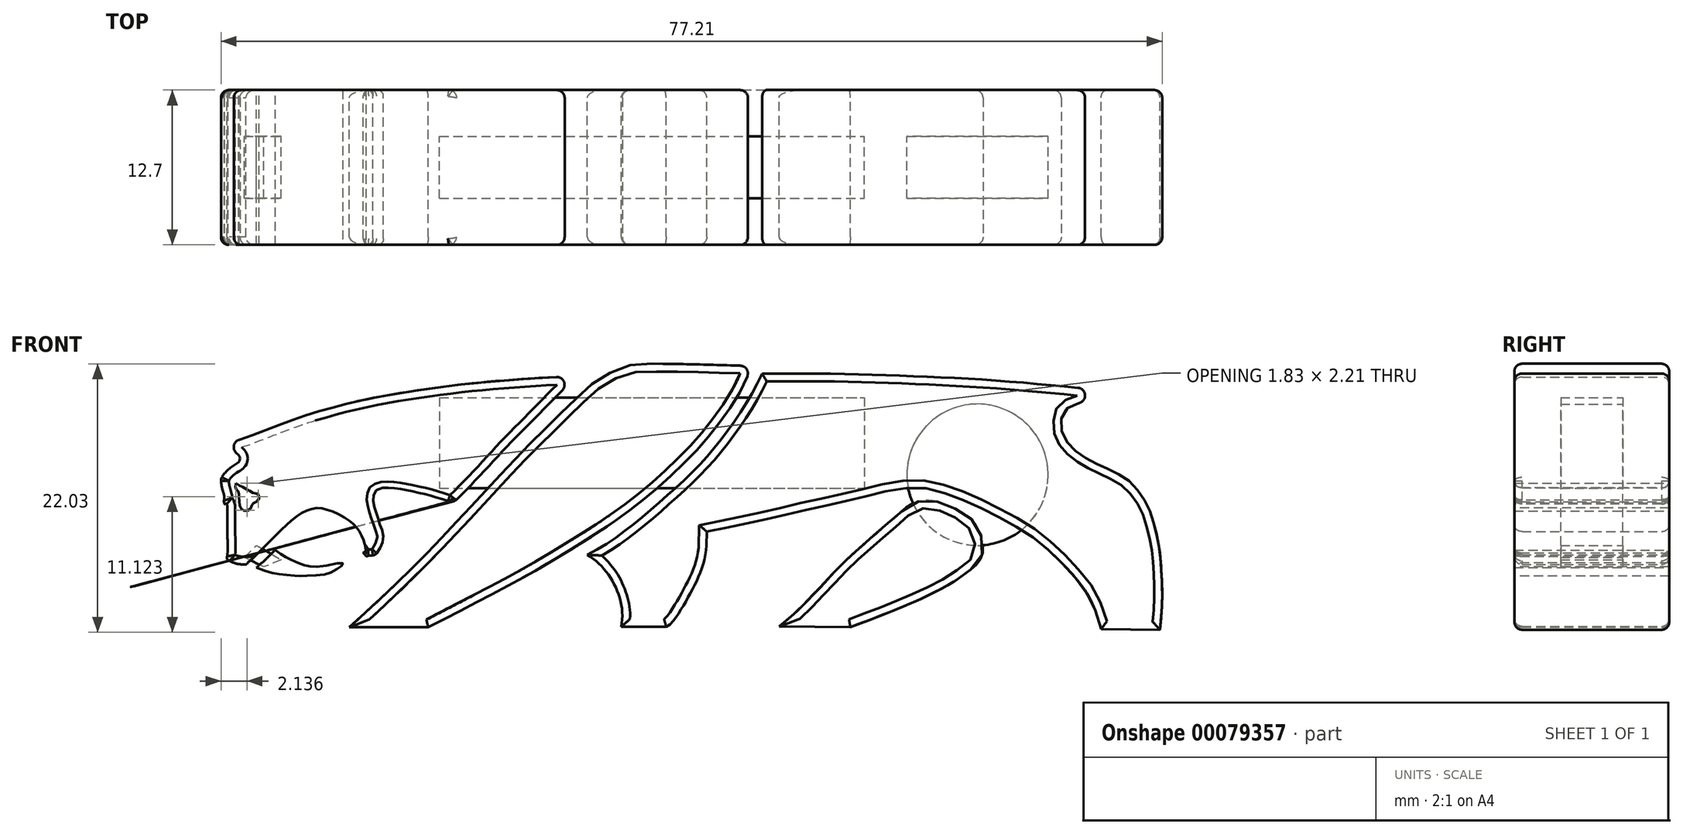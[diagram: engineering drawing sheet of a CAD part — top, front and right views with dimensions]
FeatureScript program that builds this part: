
annotation { "Feature Type Name" : "Feature", "Feature Type Description" : "" }
export const myFeature = defineFeature(function(context is Context, id is Id, definition is map)
    precondition{}
    {
        {
            var Q0;
            Q0=qCreatedBy(makeId("Front.planeOp"),FACE);
            var sketch = newSketch(context, id + "F0", { "sketchPlane" : qUnion([Q0])});
            skFitSpline(sketch, "E0", {"points": [v(-38.9, 16.63) * mm, v(-38.37, 16.66) * mm, v(-37.5, 16.88) * mm, v(-34.83, 17.89) * mm, v(-32.87, 18.61) * mm, v(-30.82, 19.24) * mm, v(-28.43, 19.87) * mm, v(-25.9, 20.4) * mm, v(-23.7, 20.77) * mm, v(-20.63, 21.2) * mm, v(-18, 21.5) * mm, v(-15.26, 21.73) * mm, v(-10.09, 22.05) * mm, v(-10.06, 22.05) * mm], "startDerivative": vector(13.14, 0.1) * mm, "endDerivative": vector(1.31, -0.1) * mm});
            skFitSpline(sketch, "E1", {"points": [v(-20.18, 11.64) * mm, v(-18.27, 13.57) * mm, v(-16.09, 15.93) * mm, v(-13.45, 18.61) * mm, v(-12.15, 19.94) * mm, v(-10.06, 22.05) * mm], "startDerivative": vector(9.83, 9.74) * mm, "endDerivative": vector(11.12, 11.22) * mm});
            skFitSpline(sketch, "E2", {"points": [v(-37.18, 6.58) * mm, v(-35.83, 7.86) * mm, v(-34.37, 9.34) * mm, v(-33.64, 10) * mm, v(-32.91, 10.62) * mm, v(-32.26, 10.97) * mm, v(-31.76, 11.15) * mm, v(-31.13, 11.2) * mm, v(-30.53, 11.07) * mm, v(-29.85, 10.82) * mm, v(-28.97, 10.34) * mm, v(-28.52, 10.02) * mm, v(-28.05, 9.54) * mm, v(-27.85, 9.24) * mm, v(-27.6, 8.75) * mm, v(-27.46, 8.36) * mm, v(-27.37, 7.82) * mm, v(-27.39, 7.68) * mm, v(-27.56, 7.54) * mm], "startDerivative": vector(14.42, 13.18) * mm, "endDerivative": vector(-7, -4.12) * mm});
            skFitSpline(sketch, "E3", {"points": [v(-20.18, 11.64) * mm, v(-20.88, 11.87) * mm, v(-21.7, 12.12) * mm, v(-22.69, 12.4) * mm, v(-23.57, 12.58) * mm, v(-24.22, 12.72) * mm, v(-24.83, 12.8) * mm, v(-25.45, 12.87) * mm, v(-25.85, 12.88) * mm, v(-26.1, 12.82) * mm, v(-26.4, 12.72) * mm, v(-26.62, 12.6) * mm, v(-26.7, 12.4) * mm, v(-26.76, 12.12) * mm, v(-26.76, 11.8) * mm, v(-26.7, 11.44) * mm, v(-26.6, 11.12) * mm, v(-26.42, 10.54) * mm, v(-26.22, 9.94) * mm, v(-26.03, 9.42) * mm, v(-25.92, 9.1) * mm, v(-25.9, 8.78) * mm, v(-25.94, 8.5) * mm, v(-26.07, 8.2) * mm, v(-26.22, 7.85) * mm, v(-26.36, 7.65) * mm, v(-26.5, 7.45) * mm, v(-26.62, 7.36) * mm, v(-26.76, 7.33) * mm, v(-26.98, 7.3) * mm, v(-27.18, 7.29) * mm, v(-27.3, 7.26) * mm, v(-27.56, 7.54) * mm], "startDerivative": vector(-16.05, 5.29) * mm, "endDerivative": vector(-9.29, 12.72) * mm});
            skFitSpline(sketch, "E4", {"points": [v(-38, 13.24) * mm, v(-37.74, 13.04) * mm, v(-37.46, 12.91) * mm, v(-37.1, 12.72) * mm, v(-36.85, 12.62) * mm, v(-36.64, 12.46) * mm, v(-36.32, 12.4) * mm, v(-36.19, 12.35) * mm, v(-36.12, 12.18) * mm, v(-36.13, 11.89) * mm, v(-36.4, 11.69) * mm, v(-36.65, 11.53) * mm, v(-36.72, 11.4) * mm, v(-36.8, 11.18) * mm, v(-37, 11.01) * mm, v(-37.25, 10.97) * mm, v(-37.5, 11.07) * mm, v(-37.65, 11.3) * mm, v(-37.74, 11.56) * mm, v(-37.75, 12) * mm, v(-37.8, 12.28) * mm, v(-37.77, 12.45) * mm, v(-37.85, 12.6) * mm, v(-37.95, 12.66) * mm, v(-38, 12.8) * mm, v(-38.03, 12.93) * mm, v(-38, 13.24) * mm]});
            skFitSpline(sketch, "E5", {"points": [v(-38.9, 16.63) * mm, v(-38.72, 16.34) * mm, v(-38.31, 15.96) * mm, v(-38.04, 15.75) * mm, v(-37.79, 15.56) * mm, v(-37.7, 15.35) * mm, v(-37.68, 15.2) * mm, v(-37.79, 15) * mm, v(-37.93, 14.86) * mm, v(-38.46, 14.5) * mm, v(-38.9, 14.11) * mm, v(-39.09, 13.86) * mm, v(-39.17, 13.71) * mm, v(-39.23, 13.56) * mm, v(-39.2, 13.06) * mm, v(-39.13, 12.8) * mm, v(-39.03, 12.4) * mm, v(-38.97, 12.12) * mm, v(-38.98, 11.6) * mm, v(-38.9, 11.53) * mm, v(-38.79, 11.59) * mm, v(-38.72, 10.31) * mm, v(-38.72, 7.29) * mm, v(-38.72, 7) * mm, v(-38.1, 6.7) * mm, v(-37.74, 6.6) * mm, v(-37.18, 6.58) * mm], "startDerivative": vector(3.81, -8.13) * mm, "endDerivative": vector(13.6, -0.25) * mm});
            skFitSpline(sketch, "E6", {"points": [v(-34.8, 7.76) * mm, v(-34.12, 7.3) * mm, v(-33.5, 6.96) * mm, v(-32.6, 6.57) * mm, v(-31.95, 6.42) * mm, v(-30.83, 6.44) * mm, v(-29.26, 6.7) * mm, v(-29.27, 6.57) * mm, v(-29.4, 6.4) * mm, v(-30.11, 5.98) * mm, v(-30.92, 5.74) * mm, v(-32.35, 5.65) * mm, v(-33, 5.65) * mm, v(-34.14, 5.75) * mm, v(-35.06, 5.9) * mm, v(-36.33, 6.33) * mm], "startDerivative": vector(10.38, -7.41) * mm, "endDerivative": vector(-15.79, 5.96) * mm});
            skFitSpline(sketch, "E7", {"points": [v(4.24, 22.85) * mm, v(3.48, 20.98) * mm, v(1.1, 17.49) * mm, v(-1.44, 14.7) * mm, v(-4.3, 12.12) * mm, v(-7.57, 9.7) * mm, v(-9.68, 8.34) * mm, v(-11.33, 7.33) * mm, v(-14.15, 5.67) * mm, v(-22.23, 1.42) * mm], "startDerivative": vector(-6.95, -21) * mm, "endDerivative": vector(-51.72, -26.65) * mm});
            skFitSpline(sketch, "E8", {"points": [v(-22.23, 1.42) * mm, v(-28.7, 1.42) * mm], "startDerivative": vector(-6.47, 0) * mm, "endDerivative": vector(-6.47, 0) * mm});
            skFitSpline(sketch, "E9", {"points": [v(-28.7, 1.42) * mm, v(-24.45, 5.4) * mm, v(-19.19, 10.82) * mm, v(-15.4, 14.92) * mm, v(-12.46, 17.9) * mm, v(-10.41, 19.89) * mm, v(-9.13, 21.07) * mm, v(-8.73, 21.45) * mm, v(-8.2, 21.81) * mm, v(-7.57, 22.17) * mm, v(-7.02, 22.45) * mm, v(-6.24, 22.74) * mm, v(-5.78, 22.89) * mm, v(-4.91, 23.02) * mm, v(4.24, 22.85) * mm], "startDerivative": vector(36.28, 33.23) * mm, "endDerivative": vector(81.45, -2.6) * mm});
            skFitSpline(sketch, "E10", {"points": [v(-6.4, 1.46) * mm, v(-6.31, 2.33) * mm, v(-6.37, 3.13) * mm, v(-6.58, 4) * mm, v(-6.9, 4.8) * mm, v(-7.41, 5.7) * mm, v(-7.9, 6.3) * mm, v(-8.3, 6.74) * mm, v(-9.18, 7.37) * mm], "startDerivative": vector(0.97, 6.96) * mm, "endDerivative": vector(-6.9, 4.6) * mm});
            skFitSpline(sketch, "E11", {"points": [v(-9.18, 7.37) * mm, v(-7.44, 8.37) * mm, v(-5.91, 9.47) * mm, v(-4.28, 10.78) * mm, v(-1.95, 12.86) * mm, v(-0.32, 14.39) * mm, v(1.21, 16.1) * mm, v(2.62, 17.95) * mm, v(3.75, 19.6) * mm, v(4.43, 20.81) * mm, v(5.15, 22.24) * mm], "startDerivative": vector(18, 9.78) * mm, "endDerivative": vector(8.35, 16.75) * mm});
            skFitSpline(sketch, "E12", {"points": [v(-6.4, 1.46) * mm, v(-2.72, 1.46) * mm], "startDerivative": vector(3.68, 0) * mm, "endDerivative": vector(3.68, 0) * mm});
            skFitSpline(sketch, "E13", {"points": [v(-2.72, 1.46) * mm, v(-2.37, 1.69) * mm, v(-1.84, 2.34) * mm, v(-1.34, 3.13) * mm, v(-0.94, 3.84) * mm, v(-0.56, 4.56) * mm, v(-0.2, 5.25) * mm, v(0.25, 6.4) * mm, v(0.53, 7.47) * mm, v(0.61, 9.28) * mm], "startDerivative": vector(4.66, 2.38) * mm, "endDerivative": vector(0.17, 12.66) * mm});
            skFitSpline(sketch, "E14", {"points": [v(0.61, 9.28) * mm, v(2.65, 9.7) * mm, v(5.56, 10.3) * mm, v(8.97, 11.11) * mm, v(11.35, 11.61) * mm, v(14.12, 12.29) * mm, v(15.87, 12.7) * mm, v(16.6, 12.8) * mm, v(17.41, 12.83) * mm, v(18.3, 12.85) * mm, v(18.73, 12.82) * mm, v(19.2, 12.72) * mm, v(20.12, 12.43) * mm, v(21.28, 12.01) * mm, v(22.59, 11.46) * mm, v(23.83, 10.86) * mm, v(25.1, 10.2) * mm, v(26.3, 9.51) * mm, v(27.1, 9) * mm, v(27.87, 8.44) * mm, v(28.73, 7.68) * mm, v(29.74, 6.73) * mm, v(30.28, 6.15) * mm, v(30.83, 5.53) * mm, v(31.5, 4.68) * mm, v(32, 3.9) * mm, v(32.42, 3) * mm, v(32.97, 1.28) * mm], "startDerivative": vector(42, 8.64) * mm, "endDerivative": vector(12.4, -42.68) * mm});
            skFitSpline(sketch, "E15", {"points": [v(5.15, 22.24) * mm, v(6.89, 22.24) * mm, v(8.36, 22.24) * mm, v(10.18, 22.24) * mm, v(13.52, 22.16) * mm, v(16.4, 22.07) * mm, v(19.27, 21.95) * mm, v(22.2, 21.8) * mm, v(27.17, 21.44) * mm, v(34, 20.77) * mm], "startDerivative": vector(21.12, 0.01) * mm, "endDerivative": vector(41.87, -4.26) * mm});
            skFitSpline(sketch, "E16", {"points": [v(34, 20.77) * mm, v(33.94, 20.57) * mm, v(33.89, 20.47) * mm, v(33.7, 20.33) * mm, v(33.1, 20.17) * mm, v(32.24, 20.02) * mm, v(31.57, 19.9) * mm, v(30.76, 19.7) * mm, v(30.04, 19.29) * mm, v(29.83, 19) * mm, v(29.74, 18.74) * mm, v(29.7, 18.29) * mm, v(29.7, 18) * mm, v(29.73, 17.59) * mm, v(29.81, 17.24) * mm, v(30, 16.86) * mm, v(30.23, 16.52) * mm, v(30.64, 16.11) * mm, v(30.93, 15.86) * mm, v(31.31, 15.57) * mm, v(31.85, 15.24) * mm, v(32.57, 14.84) * mm, v(33.26, 14.53) * mm, v(33.72, 14.3) * mm, v(34.26, 14.05) * mm, v(34.8, 13.74) * mm, v(35.2, 13.47) * mm, v(35.55, 13.14) * mm, v(35.9, 12.74) * mm, v(36.24, 12.3) * mm, v(36.5, 11.9) * mm, v(36.81, 11.39) * mm, v(37.03, 10.8) * mm, v(37.16, 10.4) * mm, v(37.38, 9.6) * mm, v(37.62, 8.6) * mm, v(37.83, 7.27) * mm, v(37.94, 5.54) * mm, v(37.98, 4.1) * mm, v(37.8, 1.22) * mm], "startDerivative": vector(-3.18, -15.16) * mm, "endDerivative": vector(-4.8, -56.57) * mm});
            skFitSpline(sketch, "E17", {"points": [v(32.97, 1.28) * mm, v(37.8, 1.22) * mm], "startDerivative": vector(4.82, -0.06) * mm, "endDerivative": vector(4.82, -0.06) * mm});
            skFitSpline(sketch, "E18", {"points": [v(6.55, 1.5) * mm, v(12.4, 1.44) * mm], "startDerivative": vector(5.84, -0.06) * mm, "endDerivative": vector(5.84, -0.06) * mm});
            skFitSpline(sketch, "E19", {"points": [v(6.55, 1.5) * mm, v(7.94, 2.67) * mm, v(9.03, 3.77) * mm, v(9.91, 4.69) * mm, v(10.63, 5.46) * mm, v(11.13, 6) * mm, v(11.6, 6.5) * mm, v(13.08, 7.87) * mm, v(13.93, 8.63) * mm, v(14.71, 9.3) * mm, v(15.39, 9.9) * mm, v(15.97, 10.39) * mm, v(16.42, 10.76) * mm, v(17.02, 11.3) * mm, v(17.46, 11.56) * mm, v(18.12, 11.8) * mm, v(18.72, 11.86) * mm, v(19.36, 11.77) * mm, v(19.82, 11.63) * mm, v(20.37, 11.44) * mm, v(20.94, 11.19) * mm, v(21.69, 10.76) * mm, v(22.18, 10.42) * mm, v(22.6, 10.02) * mm, v(22.95, 9.38) * mm, v(23.14, 8.84) * mm, v(23.25, 8.37) * mm, v(23.28, 7.82) * mm, v(23.16, 7.23) * mm, v(22.72, 6.54) * mm, v(21.88, 5.86) * mm, v(20.7, 5.05) * mm, v(19.4, 4.36) * mm, v(17.84, 3.6) * mm, v(16.28, 2.95) * mm, v(14.98, 2.41) * mm, v(13.84, 1.99) * mm, v(12.4, 1.44) * mm], "startDerivative": vector(38.08, 30.48) * mm, "endDerivative": vector(-42.7, -16.34) * mm});
            skFitSpline(sketch, "E20", {"points": [v(-36.33, 6.33) * mm, v(-35.73, 6.85) * mm, v(-35.3, 7.25) * mm, v(-34.8, 7.76) * mm], "startDerivative": vector(1.8, 1.52) * mm, "endDerivative": vector(1.56, 1.6) * mm});
            skSolve(sketch);
        }
        {
            var Q0;
            Q0=makeQuery(id+"F0.imprint","IMPRINT",FACE,{"disambiguationData":[TD([[makeQuery(id+"F0.imprint","IMPRINT",EDGE,{"derivedFrom":sQuery(id+"F0.wireOp",EDGE,"E0")}),-1.0]])]});
            var Q1;
            Q1=makeQuery(id+"F0.imprint","IMPRINT",FACE,{"disambiguationData":[TD([[makeQuery(id+"F0.imprint","IMPRINT",EDGE,{"derivedFrom":sQuery(id+"F0.wireOp",EDGE,"E7")}),-1.0]])]});
            var Q2;
            Q2=makeQuery(id+"F0.imprint","IMPRINT",FACE,{"disambiguationData":[TD([[makeQuery(id+"F0.imprint","IMPRINT",EDGE,{"derivedFrom":sQuery(id+"F0.wireOp",EDGE,"E10")}),-1.0]])]});
            var Q3;
            Q3=makeQuery(id+"F0.imprint","IMPRINT",FACE,{"disambiguationData":[TD([[makeQuery(id+"F0.imprint","IMPRINT",EDGE,{"derivedFrom":sQuery(id+"F0.wireOp",EDGE,"E18")}),1.0]])]});
            var Q4;
            Q4=makeQuery(id+"F0.imprint","IMPRINT",FACE,{"disambiguationData":[TD([[makeQuery(id+"F0.imprint","IMPRINT",EDGE,{"derivedFrom":sQuery(id+"F0.wireOp",EDGE,"E6")}),-1.0]])]});
            extrude(context, id + "F1", {"entities" : qUnion([Q0, Q1, Q2, Q3, Q4]), "depth" : 6.35 * mm, "hasSecondDirection" : true, "secondDirectionOppositeDirection" : true, "secondDirectionDepth" : 6.35 * mm});
        }
        {
            var Q0;
            Q0=qCreatedBy(makeId("Front.planeOp"),FACE);
            var sketch = newSketch(context, id + "F2", { "sketchPlane" : qUnion([Q0])});
            skLineSegment(sketch, "E21.bottom", {"start": v(-21.31, 20.27) * mm, "end": v(13.55, 20.27) * mm});
            skLineSegment(sketch, "E21.top", {"start": v(-21.31, 12.84) * mm, "end": v(13.55, 12.84) * mm});
            skLineSegment(sketch, "E21.left", {"start": v(-21.31, 20.27) * mm, "end": v(-21.31, 12.84) * mm});
            skLineSegment(sketch, "E21.right", {"start": v(13.55, 20.27) * mm, "end": v(13.55, 12.84) * mm});
            skCircle(sketch, "E22", {"center": v(22.83, 13.94) * mm, "radius": 5.8 * mm});
            skLineSegment(sketch, "E23", {"start": v(-35.72, 6.37) * mm, "end": v(-37.33, 7.16) * mm});
            skLineSegment(sketch, "E24", {"start": v(-37.33, 7.16) * mm, "end": v(-36.32, 8.14) * mm});
            skLineSegment(sketch, "E25", {"start": v(-36.32, 8.14) * mm, "end": v(-34.3, 6.97) * mm});
            skLineSegment(sketch, "E26", {"start": v(-34.3, 6.97) * mm, "end": v(-35.72, 6.37) * mm});
            skSolve(sketch);
        }
        {
            var Q0;
            Q0=makeQuery(id+"F2.imprint","IMPRINT",FACE,{"disambiguationData":[TD([[makeQuery(id+"F2.imprint","IMPRINT",EDGE,{"derivedFrom":sQuery(id+"F2.wireOp",EDGE,"E21.bottom")}),-1.0]])]});
            var Q1;
            Q1=makeQuery(id+"F2.imprint","IMPRINT",FACE,{"disambiguationData":[TD([[makeQuery(id+"F2.imprint","IMPRINT",EDGE,{"derivedFrom":sQuery(id+"F2.wireOp",EDGE,"E22")}),1.0]])]});
            var Q2;
            Q2=makeQuery(id+"F2.imprint","IMPRINT",FACE,{"disambiguationData":[TD([[makeQuery(id+"F2.imprint","IMPRINT",EDGE,{"derivedFrom":sQuery(id+"F2.wireOp",EDGE,"E23")}),-1.0]])]});
            extrude(context, id + "F3", {"entities" : qUnion([Q0, Q1, Q2]), "depth" : 2.54 * mm, "hasSecondDirection" : true, "secondDirectionOppositeDirection" : true, "secondDirectionDepth" : 2.54 * mm});
        }
        {
            var Q0;
            Q0=makeQuery(id+"F1.opExtrude","CAP_EDGE",EDGE,{"disambiguationData":[OSD([sQuery(id+"F0.wireOp",EDGE,"E9")])],"isStart":false});
            var Q1;
            Q1=makeQuery(id+"F1.opExtrude","CAP_EDGE",EDGE,{"disambiguationData":[OSD([sQuery(id+"F0.wireOp",EDGE,"E7")])],"isStart":false});
            var Q2;
            Q2=makeQuery(id+"F1.opExtrude","CAP_EDGE",EDGE,{"disambiguationData":[OSD([sQuery(id+"F0.wireOp",EDGE,"E8")])],"isStart":false});
            var Q3;
            Q3=makeQuery(id+"F1.opExtrude","CAP_EDGE",EDGE,{"disambiguationData":[OSD([sQuery(id+"F0.wireOp",EDGE,"E10")])],"isStart":false});
            var Q4;
            Q4=makeQuery(id+"F1.opExtrude","CAP_EDGE",EDGE,{"disambiguationData":[OSD([sQuery(id+"F0.wireOp",EDGE,"E11")])],"isStart":false});
            var Q5;
            Q5=makeQuery(id+"F1.opExtrude","CAP_EDGE",EDGE,{"disambiguationData":[OSD([sQuery(id+"F0.wireOp",EDGE,"E13")])],"isStart":false});
            var Q6;
            Q6=makeQuery(id+"F1.opExtrude","CAP_EDGE",EDGE,{"disambiguationData":[OSD([sQuery(id+"F0.wireOp",EDGE,"E12")])],"isStart":false});
            var Q7;
            Q7=makeQuery(id+"F1.opExtrude","CAP_EDGE",EDGE,{"disambiguationData":[OSD([sQuery(id+"F0.wireOp",EDGE,"E14")])],"isStart":false});
            var Q8;
            Q8=makeQuery(id+"F1.opExtrude","CAP_EDGE",EDGE,{"disambiguationData":[OSD([sQuery(id+"F0.wireOp",EDGE,"E15")])],"isStart":false});
            var Q9;
            Q9=makeQuery(id+"F1.opExtrude","CAP_EDGE",EDGE,{"disambiguationData":[OSD([sQuery(id+"F0.wireOp",EDGE,"E17")])],"isStart":false});
            var Q10;
            Q10=makeQuery(id+"F1.opExtrude","SWEPT_EDGE",EDGE,{"disambiguationData":[OSD([sQuery(id+"F0.wireOp",EDGE,"E15"),sQuery(id+"F0.wireOp",EDGE,"E16")])]});
            var Q11;
            Q11=makeQuery(id+"F1.opExtrude","CAP_EDGE",EDGE,{"disambiguationData":[OSD([sQuery(id+"F0.wireOp",EDGE,"E16")])],"isStart":false});
            var Q12;
            Q12=makeQuery(id+"F1.opExtrude","CAP_EDGE",EDGE,{"disambiguationData":[OSD([sQuery(id+"F0.wireOp",EDGE,"E19")])],"isStart":false});
            var Q13;
            Q13=makeQuery(id+"F1.opExtrude","CAP_EDGE",EDGE,{"disambiguationData":[OSD([sQuery(id+"F0.wireOp",EDGE,"E18")])],"isStart":false});
            var Q14;
            Q14=makeQuery(id+"F1.opExtrude","CAP_EDGE",EDGE,{"disambiguationData":[OSD([sQuery(id+"F0.wireOp",EDGE,"E1")])],"isStart":false});
            var Q15;
            Q15=makeQuery(id+"F1.opExtrude","SWEPT_EDGE",EDGE,{"disambiguationData":[OSD([sQuery(id+"F0.wireOp",EDGE,"E7"),sQuery(id+"F0.wireOp",EDGE,"E9")])]});
            var Q16;
            Q16=makeQuery(id+"F1.opExtrude","SWEPT_EDGE",EDGE,{"disambiguationData":[OSD([sQuery(id+"F0.wireOp",EDGE,"E0"),sQuery(id+"F0.wireOp",EDGE,"E1")])]});
            var Q17;
            Q17=makeQuery(id+"F1.opExtrude","SWEPT_EDGE",EDGE,{"disambiguationData":[OSD([sQuery(id+"F0.wireOp",EDGE,"E1"),sQuery(id+"F0.wireOp",EDGE,"E3")])]});
            var Q18;
            Q18=makeQuery(id+"F1.opExtrude","CAP_EDGE",EDGE,{"disambiguationData":[OSD([sQuery(id+"F0.wireOp",EDGE,"E0")])],"isStart":false});
            var Q19;
            Q19=makeQuery(id+"F1.opExtrude","SWEPT_EDGE",EDGE,{"disambiguationData":[OSD([sQuery(id+"F0.wireOp",EDGE,"E0"),sQuery(id+"F0.wireOp",EDGE,"E5")])]});
            var Q20;
            Q20=makeQuery(id+"F1.opExtrude","CAP_EDGE",EDGE,{"disambiguationData":[OSD([sQuery(id+"F0.wireOp",EDGE,"E5")])],"isStart":false});
            fillet(context, id + "F4", {"entities" : qUnion([Q0, Q1, Q2, Q3, Q4, Q5, Q6, Q7, Q8, Q9, Q10, Q11, Q12, Q13, Q14, Q15, Q16, Q17, Q18, Q19, Q20]), "radius" : 0.64 * mm, "tangentPropagation" : true, "allowEdgeOverflow" : false});
        }
        {
            var Q0;
            Q0=makeQuery(id+"F1.opExtrude","CAP_EDGE",EDGE,{"disambiguationData":[OSD([sQuery(id+"F0.wireOp",EDGE,"E15")])],"isStart":true});
            var Q1;
            Q1=makeQuery(id+"F1.opExtrude","CAP_EDGE",EDGE,{"disambiguationData":[OSD([sQuery(id+"F0.wireOp",EDGE,"E17")])],"isStart":true});
            var Q2;
            Q2=makeQuery(id+"F1.opExtrude","CAP_EDGE",EDGE,{"disambiguationData":[OSD([sQuery(id+"F0.wireOp",EDGE,"E14")])],"isStart":true});
            var Q3;
            Q3=makeQuery(id+"F1.opExtrude","CAP_EDGE",EDGE,{"disambiguationData":[OSD([sQuery(id+"F0.wireOp",EDGE,"E13")])],"isStart":true});
            var Q4;
            Q4=makeQuery(id+"F1.opExtrude","CAP_EDGE",EDGE,{"disambiguationData":[OSD([sQuery(id+"F0.wireOp",EDGE,"E12")])],"isStart":true});
            var Q5;
            Q5=makeQuery(id+"F1.opExtrude","CAP_EDGE",EDGE,{"disambiguationData":[OSD([sQuery(id+"F0.wireOp",EDGE,"E10")])],"isStart":true});
            var Q6;
            Q6=makeQuery(id+"F1.opExtrude","CAP_EDGE",EDGE,{"disambiguationData":[OSD([sQuery(id+"F0.wireOp",EDGE,"E11")])],"isStart":true});
            var Q7;
            Q7=makeQuery(id+"F1.opExtrude","CAP_EDGE",EDGE,{"disambiguationData":[OSD([sQuery(id+"F0.wireOp",EDGE,"E19")])],"isStart":true});
            var Q8;
            Q8=makeQuery(id+"F1.opExtrude","CAP_EDGE",EDGE,{"disambiguationData":[OSD([sQuery(id+"F0.wireOp",EDGE,"E18")])],"isStart":true});
            var Q9;
            Q9=makeQuery(id+"F1.opExtrude","CAP_EDGE",EDGE,{"disambiguationData":[OSD([sQuery(id+"F0.wireOp",EDGE,"E7")])],"isStart":true});
            var Q10;
            Q10=makeQuery(id+"F1.opExtrude","CAP_EDGE",EDGE,{"disambiguationData":[OSD([sQuery(id+"F0.wireOp",EDGE,"E9")])],"isStart":true});
            var Q11;
            Q11=makeQuery(id+"F1.opExtrude","CAP_EDGE",EDGE,{"disambiguationData":[OSD([sQuery(id+"F0.wireOp",EDGE,"E8")])],"isStart":true});
            var Q12;
            Q12=makeQuery(id+"F1.opExtrude","CAP_EDGE",EDGE,{"disambiguationData":[OSD([sQuery(id+"F0.wireOp",EDGE,"E1")])],"isStart":true});
            fillet(context, id + "F5", {"entities" : qUnion([Q0, Q1, Q2, Q3, Q4, Q5, Q6, Q7, Q8, Q9, Q10, Q11, Q12]), "radius" : 0.64 * mm, "tangentPropagation" : true, "allowEdgeOverflow" : false});
        }
        {
            var Q0;
            Q0=makeQuery(id+"F1.opExtrude","CAP_EDGE",EDGE,{"disambiguationData":[OSD([sQuery(id+"F0.wireOp",EDGE,"E3")])],"isStart":true});
            var Q1;
            Q1=makeQuery(id+"F1.opExtrude","CAP_EDGE",EDGE,{"disambiguationData":[OSD([sQuery(id+"F0.wireOp",EDGE,"E3")])],"isStart":false});
            fillet(context, id + "F6", {"entities" : qUnion([Q0, Q1]), "radius" : 0.5 * mm, "tangentPropagation" : true, "allowEdgeOverflow" : false});
        }
    });
